# Revit family: vanity unit with 2 drawers for consoles with bowl
name_source: partatom
category: Furniture
units: mm (PartAtom-declared; Revit-internal decimal feet)

## family parameters
Always vertical = Yes
Cut with Voids When Loaded = No
OmniClass Number = 23.21.19.15.33.13
Room Calculation Point = No
Shared = Yes
Work Plane-Based = No

## types (72) — shared parameters
BIMOBJECT = Sanitary: Compound units
CATALOG = Hansgrohe
DESIGN = Germany
ETIM = EC011381 | Bathroom furniture set
IFC = Furnishing element
MASTERFORMAT = 12 35 30.23 | Bathroom Casework
Manufacturer = Hansgrohe
NBSYN = $BASENUMBER.-$ARTNR.-$OBERFLAECHE.-$SURFACE.-$LODLEVEL.
NN = Vanity unit with 2 drawers for consoles with bowl
OBJECTTYPE = Object (single object)
OMNICLASS = 23-21 19 15 33 13 | Residential Bathroom Specialty Casework
PRODUCTFAMILY = Xelu Q
PRODUCTGROUP = vanity unit
PRODUCTURL = https://pro.hansgrohe.com
REGIONSET = Worldwide
UNICLASS2015 = Pr_40_30_78_05 | Bathroom furniture
UNICLASS_2015_CODE = 40_30_78_05
UNIFORMATII = E2010 | Fixed Furnishings
UNSPSC = 56 | Furniture and Furnishings
etim7_EC011381 = EC011381

## per-type parameters (varying)
| type | ARTNR | BASENUMBER | GTINCODE | L | LINA | LODLEVEL | Model | NAME | NB | OBERFLAECHE | PERMALINK | SURFACE | WEIGHT |
| Vanity unit 1180_550 with 2 drawers for consoles with bowl-54082000-High Gloss White-CHROME-200 | 54082000 | Vanity unit 1180/550 with 2 drawers for consoles with bowl | 4059625456699 | 1180 | Vanity unit 1180/550 with 2 drawers for consoles with bowl-54082000-High Gloss White-CHROME-200 | 200 | Vanity unit 1180/550 with 2 drawers for consoles with bowl-54082000-High Gloss White-CHROME-200 | Xelu Q Vanity unit High Gloss White 1180/550 with 2 drawers for consoles with bowl | Vanity unit 1180/550 with 2 drawers for consoles with bowl-54082000-High Gloss White-CHROME-200 | High Gloss White | 54082XXX | CHROME | 42.7 |
| Vanity unit 1180_550 with 2 drawers for consoles with bowl-54082000-High Gloss White-CHROME-400 | 54082000 | Vanity unit 1180/550 with 2 drawers for consoles with bowl | 4059625456699 | 1180 | Vanity unit 1180/550 with 2 drawers for consoles with bowl-54082000-High Gloss White-CHROME-400 | 400 | Vanity unit 1180/550 with 2 drawers for consoles with bowl-54082000-High Gloss White-CHROME-400 | Xelu Q Vanity unit High Gloss White 1180/550 with 2 drawers for consoles with bowl | Vanity unit 1180/550 with 2 drawers for consoles with bowl-54082000-High Gloss White-CHROME-400 | High Gloss White | 54082XXX | CHROME | 42.7 |
| Vanity unit 1180_550 with 2 drawers for consoles with bowl-54082670-High Gloss White-MATT_BLACK-200 | 54082670 | Vanity unit 1180/550 with 2 drawers for consoles with bowl | 4059625456699 | 1180 | Vanity unit 1180/550 with 2 drawers for consoles with bowl-54082670-High Gloss White-MATT_BLACK-200 | 200 | Vanity unit 1180/550 with 2 drawers for consoles with bowl-54082670-High Gloss White-MATT_BLACK-200 | Xelu Q Vanity unit High Gloss White 1180/550 with 2 drawers for consoles with bowl | Vanity unit 1180/550 with 2 drawers for consoles with bowl-54082670-High Gloss White-MATT_BLACK-200 | High Gloss White | 54082XXX | MATT_BLACK | 42.7 |
| Vanity unit 1180_550 with 2 drawers for consoles with bowl-54082670-High Gloss White-MATT_BLACK-400 | 54082670 | Vanity unit 1180/550 with 2 drawers for consoles with bowl | 4059625456699 | 1180 | Vanity unit 1180/550 with 2 drawers for consoles with bowl-54082670-High Gloss White-MATT_BLACK-400 | 400 | Vanity unit 1180/550 with 2 drawers for consoles with bowl-54082670-High Gloss White-MATT_BLACK-400 | Xelu Q Vanity unit High Gloss White 1180/550 with 2 drawers for consoles with bowl | Vanity unit 1180/550 with 2 drawers for consoles with bowl-54082670-High Gloss White-MATT_BLACK-400 | High Gloss White | 54082XXX | MATT_BLACK | 42.7 |
| Vanity unit 1180_550 with 2 drawers for consoles with bowl-54082700-High Gloss White-MATT_WHITE-200 | 54082700 | Vanity unit 1180/550 with 2 drawers for consoles with bowl | 4059625456699 | 1180 | Vanity unit 1180/550 with 2 drawers for consoles with bowl-54082700-High Gloss White-MATT_WHITE-200 | 200 | Vanity unit 1180/550 with 2 drawers for consoles with bowl-54082700-High Gloss White-MATT_WHITE-200 | Xelu Q Vanity unit High Gloss White 1180/550 with 2 drawers for consoles with bowl | Vanity unit 1180/550 with 2 drawers for consoles with bowl-54082700-High Gloss White-MATT_WHITE-200 | High Gloss White | 54082XXX | MATT_WHITE | 42.7 |
| Vanity unit 1180_550 with 2 drawers for consoles with bowl-54082700-High Gloss White-MATT_WHITE-400 | 54082700 | Vanity unit 1180/550 with 2 drawers for consoles with bowl | 4059625456699 | 1180 | Vanity unit 1180/550 with 2 drawers for consoles with bowl-54082700-High Gloss White-MATT_WHITE-400 | 400 | Vanity unit 1180/550 with 2 drawers for consoles with bowl-54082700-High Gloss White-MATT_WHITE-400 | Xelu Q Vanity unit High Gloss White 1180/550 with 2 drawers for consoles with bowl | Vanity unit 1180/550 with 2 drawers for consoles with bowl-54082700-High Gloss White-MATT_WHITE-400 | High Gloss White | 54082XXX | MATT_WHITE | 42.7 |
| Vanity unit 1180_550 with 2 drawers for consoles with bowl-54083000-Diamond Matt Grey-CHROME-200 | 54083000 | Vanity unit 1180/550 with 2 drawers for consoles with bowl | 4059625456668 | 1180 | Vanity unit 1180/550 with 2 drawers for consoles with bowl-54083000-Diamond Matt Grey-CHROME-200 | 200 | Vanity unit 1180/550 with 2 drawers for consoles with bowl-54083000-Diamond Matt Grey-CHROME-200 | Xelu Q Vanity unit Diamond Matt Grey 1180/550 with 2 drawers for consoles with bowl | Vanity unit 1180/550 with 2 drawers for consoles with bowl-54083000-Diamond Matt Grey-CHROME-200 | Diamond Matt Grey | 54083XXX | CHROME | 42.7 |
| Vanity unit 1180_550 with 2 drawers for consoles with bowl-54083000-Diamond Matt Grey-CHROME-400 | 54083000 | Vanity unit 1180/550 with 2 drawers for consoles with bowl | 4059625456668 | 1180 | Vanity unit 1180/550 with 2 drawers for consoles with bowl-54083000-Diamond Matt Grey-CHROME-400 | 400 | Vanity unit 1180/550 with 2 drawers for consoles with bowl-54083000-Diamond Matt Grey-CHROME-400 | Xelu Q Vanity unit Diamond Matt Grey 1180/550 with 2 drawers for consoles with bowl | Vanity unit 1180/550 with 2 drawers for consoles with bowl-54083000-Diamond Matt Grey-CHROME-400 | Diamond Matt Grey | 54083XXX | CHROME | 42.7 |
| Vanity unit 1180_550 with 2 drawers for consoles with bowl-54083670-Diamond Matt Grey-MATT_BLACK-200 | 54083670 | Vanity unit 1180/550 with 2 drawers for consoles with bowl | 4059625456668 | 1180 | Vanity unit 1180/550 with 2 drawers for consoles with bowl-54083670-Diamond Matt Grey-MATT_BLACK-200 | 200 | Vanity unit 1180/550 with 2 drawers for consoles with bowl-54083670-Diamond Matt Grey-MATT_BLACK-200 | Xelu Q Vanity unit Diamond Matt Grey 1180/550 with 2 drawers for consoles with bowl | Vanity unit 1180/550 with 2 drawers for consoles with bowl-54083670-Diamond Matt Grey-MATT_BLACK-200 | Diamond Matt Grey | 54083XXX | MATT_BLACK | 42.7 |
| Vanity unit 1180_550 with 2 drawers for consoles with bowl-54083670-Diamond Matt Grey-MATT_BLACK-400 | 54083670 | Vanity unit 1180/550 with 2 drawers for consoles with bowl | 4059625456668 | 1180 | Vanity unit 1180/550 with 2 drawers for consoles with bowl-54083670-Diamond Matt Grey-MATT_BLACK-400 | 400 | Vanity unit 1180/550 with 2 drawers for consoles with bowl-54083670-Diamond Matt Grey-MATT_BLACK-400 | Xelu Q Vanity unit Diamond Matt Grey 1180/550 with 2 drawers for consoles with bowl | Vanity unit 1180/550 with 2 drawers for consoles with bowl-54083670-Diamond Matt Grey-MATT_BLACK-400 | Diamond Matt Grey | 54083XXX | MATT_BLACK | 42.7 |
| Vanity unit 1180_550 with 2 drawers for consoles with bowl-54083700-Diamond Matt Grey-MATT_WHITE-200 | 54083700 | Vanity unit 1180/550 with 2 drawers for consoles with bowl | 4059625456668 | 1180 | Vanity unit 1180/550 with 2 drawers for consoles with bowl-54083700-Diamond Matt Grey-MATT_WHITE-200 | 200 | Vanity unit 1180/550 with 2 drawers for consoles with bowl-54083700-Diamond Matt Grey-MATT_WHITE-200 | Xelu Q Vanity unit Diamond Matt Grey 1180/550 with 2 drawers for consoles with bowl | Vanity unit 1180/550 with 2 drawers for consoles with bowl-54083700-Diamond Matt Grey-MATT_WHITE-200 | Diamond Matt Grey | 54083XXX | MATT_WHITE | 42.7 |
| Vanity unit 1180_550 with 2 drawers for consoles with bowl-54083700-Diamond Matt Grey-MATT_WHITE-400 | 54083700 | Vanity unit 1180/550 with 2 drawers for consoles with bowl | 4059625456668 | 1180 | Vanity unit 1180/550 with 2 drawers for consoles with bowl-54083700-Diamond Matt Grey-MATT_WHITE-400 | 400 | Vanity unit 1180/550 with 2 drawers for consoles with bowl-54083700-Diamond Matt Grey-MATT_WHITE-400 | Xelu Q Vanity unit Diamond Matt Grey 1180/550 with 2 drawers for consoles with bowl | Vanity unit 1180/550 with 2 drawers for consoles with bowl-54083700-Diamond Matt Grey-MATT_WHITE-400 | Diamond Matt Grey | 54083XXX | MATT_WHITE | 42.7 |
| Vanity unit 1180_550 with 2 drawers for consoles with bowl-54084000-Natural Oak-CHROME-200 | 54084000 | Vanity unit 1180/550 with 2 drawers for consoles with bowl | 4059625457030 | 1180 | Vanity unit 1180/550 with 2 drawers for consoles with bowl-54084000-Natural Oak-CHROME-200 | 200 | Vanity unit 1180/550 with 2 drawers for consoles with bowl-54084000-Natural Oak-CHROME-200 | Xelu Q Vanity unit Natural Oak 1180/550 with 2 drawers for consoles with bowl | Vanity unit 1180/550 with 2 drawers for consoles with bowl-54084000-Natural Oak-CHROME-200 | Natural Oak | 54084XXX | CHROME | 42.7 |
| Vanity unit 1180_550 with 2 drawers for consoles with bowl-54084000-Natural Oak-CHROME-400 | 54084000 | Vanity unit 1180/550 with 2 drawers for consoles with bowl | 4059625457030 | 1180 | Vanity unit 1180/550 with 2 drawers for consoles with bowl-54084000-Natural Oak-CHROME-400 | 400 | Vanity unit 1180/550 with 2 drawers for consoles with bowl-54084000-Natural Oak-CHROME-400 | Xelu Q Vanity unit Natural Oak 1180/550 with 2 drawers for consoles with bowl | Vanity unit 1180/550 with 2 drawers for consoles with bowl-54084000-Natural Oak-CHROME-400 | Natural Oak | 54084XXX | CHROME | 42.7 |
| Vanity unit 1180_550 with 2 drawers for consoles with bowl-54084670-Natural Oak-MATT_BLACK-200 | 54084670 | Vanity unit 1180/550 with 2 drawers for consoles with bowl | 4059625457030 | 1180 | Vanity unit 1180/550 with 2 drawers for consoles with bowl-54084670-Natural Oak-MATT_BLACK-200 | 200 | Vanity unit 1180/550 with 2 drawers for consoles with bowl-54084670-Natural Oak-MATT_BLACK-200 | Xelu Q Vanity unit Natural Oak 1180/550 with 2 drawers for consoles with bowl | Vanity unit 1180/550 with 2 drawers for consoles with bowl-54084670-Natural Oak-MATT_BLACK-200 | Natural Oak | 54084XXX | MATT_BLACK | 42.7 |
| Vanity unit 1180_550 with 2 drawers for consoles with bowl-54084670-Natural Oak-MATT_BLACK-400 | 54084670 | Vanity unit 1180/550 with 2 drawers for consoles with bowl | 4059625457030 | 1180 | Vanity unit 1180/550 with 2 drawers for consoles with bowl-54084670-Natural Oak-MATT_BLACK-400 | 400 | Vanity unit 1180/550 with 2 drawers for consoles with bowl-54084670-Natural Oak-MATT_BLACK-400 | Xelu Q Vanity unit Natural Oak 1180/550 with 2 drawers for consoles with bowl | Vanity unit 1180/550 with 2 drawers for consoles with bowl-54084670-Natural Oak-MATT_BLACK-400 | Natural Oak | 54084XXX | MATT_BLACK | 42.7 |
| Vanity unit 1180_550 with 2 drawers for consoles with bowl-54084700-Natural Oak-MATT_WHITE-200 | 54084700 | Vanity unit 1180/550 with 2 drawers for consoles with bowl | 4059625457030 | 1180 | Vanity unit 1180/550 with 2 drawers for consoles with bowl-54084700-Natural Oak-MATT_WHITE-200 | 200 | Vanity unit 1180/550 with 2 drawers for consoles with bowl-54084700-Natural Oak-MATT_WHITE-200 | Xelu Q Vanity unit Natural Oak 1180/550 with 2 drawers for consoles with bowl | Vanity unit 1180/550 with 2 drawers for consoles with bowl-54084700-Natural Oak-MATT_WHITE-200 | Natural Oak | 54084XXX | MATT_WHITE | 42.7 |
| Vanity unit 1180_550 with 2 drawers for consoles with bowl-54084700-Natural Oak-MATT_WHITE-400 | 54084700 | Vanity unit 1180/550 with 2 drawers for consoles with bowl | 4059625457030 | 1180 | Vanity unit 1180/550 with 2 drawers for consoles with bowl-54084700-Natural Oak-MATT_WHITE-400 | 400 | Vanity unit 1180/550 with 2 drawers for consoles with bowl-54084700-Natural Oak-MATT_WHITE-400 | Xelu Q Vanity unit Natural Oak 1180/550 with 2 drawers for consoles with bowl | Vanity unit 1180/550 with 2 drawers for consoles with bowl-54084700-Natural Oak-MATT_WHITE-400 | Natural Oak | 54084XXX | MATT_WHITE | 42.7 |
| Vanity unit 1180_550 with 2 drawers for consoles with bowl-54085000-Dark Walnut-CHROME-200 | 54085000 | Vanity unit 1180/550 with 2 drawers for consoles with bowl | 4059625457009 | 1180 | Vanity unit 1180/550 with 2 drawers for consoles with bowl-54085000-Dark Walnut-CHROME-200 | 200 | Vanity unit 1180/550 with 2 drawers for consoles with bowl-54085000-Dark Walnut-CHROME-200 | Xelu Q Vanity unit Dark Walnut 1180/550 with 2 drawers for consoles with bowl | Vanity unit 1180/550 with 2 drawers for consoles with bowl-54085000-Dark Walnut-CHROME-200 | Dark Walnut | 54085XXX | CHROME | 42.7 |
| Vanity unit 1180_550 with 2 drawers for consoles with bowl-54085000-Dark Walnut-CHROME-400 | 54085000 | Vanity unit 1180/550 with 2 drawers for consoles with bowl | 4059625457009 | 1180 | Vanity unit 1180/550 with 2 drawers for consoles with bowl-54085000-Dark Walnut-CHROME-400 | 400 | Vanity unit 1180/550 with 2 drawers for consoles with bowl-54085000-Dark Walnut-CHROME-400 | Xelu Q Vanity unit Dark Walnut 1180/550 with 2 drawers for consoles with bowl | Vanity unit 1180/550 with 2 drawers for consoles with bowl-54085000-Dark Walnut-CHROME-400 | Dark Walnut | 54085XXX | CHROME | 42.7 |
| Vanity unit 1180_550 with 2 drawers for consoles with bowl-54085670-Dark Walnut-MATT_BLACK-200 | 54085670 | Vanity unit 1180/550 with 2 drawers for consoles with bowl | 4059625457009 | 1180 | Vanity unit 1180/550 with 2 drawers for consoles with bowl-54085670-Dark Walnut-MATT_BLACK-200 | 200 | Vanity unit 1180/550 with 2 drawers for consoles with bowl-54085670-Dark Walnut-MATT_BLACK-200 | Xelu Q Vanity unit Dark Walnut 1180/550 with 2 drawers for consoles with bowl | Vanity unit 1180/550 with 2 drawers for consoles with bowl-54085670-Dark Walnut-MATT_BLACK-200 | Dark Walnut | 54085XXX | MATT_BLACK | 42.7 |
| Vanity unit 1180_550 with 2 drawers for consoles with bowl-54085670-Dark Walnut-MATT_BLACK-400 | 54085670 | Vanity unit 1180/550 with 2 drawers for consoles with bowl | 4059625457009 | 1180 | Vanity unit 1180/550 with 2 drawers for consoles with bowl-54085670-Dark Walnut-MATT_BLACK-400 | 400 | Vanity unit 1180/550 with 2 drawers for consoles with bowl-54085670-Dark Walnut-MATT_BLACK-400 | Xelu Q Vanity unit Dark Walnut 1180/550 with 2 drawers for consoles with bowl | Vanity unit 1180/550 with 2 drawers for consoles with bowl-54085670-Dark Walnut-MATT_BLACK-400 | Dark Walnut | 54085XXX | MATT_BLACK | 42.7 |
| Vanity unit 1180_550 with 2 drawers for consoles with bowl-54085700-Dark Walnut-MATT_WHITE-200 | 54085700 | Vanity unit 1180/550 with 2 drawers for consoles with bowl | 4059625457009 | 1180 | Vanity unit 1180/550 with 2 drawers for consoles with bowl-54085700-Dark Walnut-MATT_WHITE-200 | 200 | Vanity unit 1180/550 with 2 drawers for consoles with bowl-54085700-Dark Walnut-MATT_WHITE-200 | Xelu Q Vanity unit Dark Walnut 1180/550 with 2 drawers for consoles with bowl | Vanity unit 1180/550 with 2 drawers for consoles with bowl-54085700-Dark Walnut-MATT_WHITE-200 | Dark Walnut | 54085XXX | MATT_WHITE | 42.7 |
| Vanity unit 1180_550 with 2 drawers for consoles with bowl-54085700-Dark Walnut-MATT_WHITE-400 | 54085700 | Vanity unit 1180/550 with 2 drawers for consoles with bowl | 4059625457009 | 1180 | Vanity unit 1180/550 with 2 drawers for consoles with bowl-54085700-Dark Walnut-MATT_WHITE-400 | 400 | Vanity unit 1180/550 with 2 drawers for consoles with bowl-54085700-Dark Walnut-MATT_WHITE-400 | Xelu Q Vanity unit Dark Walnut 1180/550 with 2 drawers for consoles with bowl | Vanity unit 1180/550 with 2 drawers for consoles with bowl-54085700-Dark Walnut-MATT_WHITE-400 | Dark Walnut | 54085XXX | MATT_WHITE | 42.7 |
| Vanity unit 780_550 with 2 drawers for consoles with bowl-54074000-High Gloss White-CHROME-200 | 54074000 | Vanity unit 780/550 with 2 drawers for consoles with bowl | 4059625456538 | 780 | Vanity unit 780/550 with 2 drawers for consoles with bowl-54074000-High Gloss White-CHROME-200 | 200 | Vanity unit 780/550 with 2 drawers for consoles with bowl-54074000-High Gloss White-CHROME-200 | Xelu Q Vanity unit High Gloss White 780/550 with 2 drawers for consoles with bowl | Vanity unit 780/550 with 2 drawers for consoles with bowl-54074000-High Gloss White-CHROME-200 | High Gloss White | 54074XXX | CHROME | 31.3 |
| Vanity unit 780_550 with 2 drawers for consoles with bowl-54074000-High Gloss White-CHROME-400 | 54074000 | Vanity unit 780/550 with 2 drawers for consoles with bowl | 4059625456538 | 780 | Vanity unit 780/550 with 2 drawers for consoles with bowl-54074000-High Gloss White-CHROME-400 | 400 | Vanity unit 780/550 with 2 drawers for consoles with bowl-54074000-High Gloss White-CHROME-400 | Xelu Q Vanity unit High Gloss White 780/550 with 2 drawers for consoles with bowl | Vanity unit 780/550 with 2 drawers for consoles with bowl-54074000-High Gloss White-CHROME-400 | High Gloss White | 54074XXX | CHROME | 31.3 |
| Vanity unit 780_550 with 2 drawers for consoles with bowl-54074670-High Gloss White-MATT_BLACK-200 | 54074670 | Vanity unit 780/550 with 2 drawers for consoles with bowl | 4059625456538 | 780 | Vanity unit 780/550 with 2 drawers for consoles with bowl-54074670-High Gloss White-MATT_BLACK-200 | 200 | Vanity unit 780/550 with 2 drawers for consoles with bowl-54074670-High Gloss White-MATT_BLACK-200 | Xelu Q Vanity unit High Gloss White 780/550 with 2 drawers for consoles with bowl | Vanity unit 780/550 with 2 drawers for consoles with bowl-54074670-High Gloss White-MATT_BLACK-200 | High Gloss White | 54074XXX | MATT_BLACK | 31.3 |
| Vanity unit 780_550 with 2 drawers for consoles with bowl-54074670-High Gloss White-MATT_BLACK-400 | 54074670 | Vanity unit 780/550 with 2 drawers for consoles with bowl | 4059625456538 | 780 | Vanity unit 780/550 with 2 drawers for consoles with bowl-54074670-High Gloss White-MATT_BLACK-400 | 400 | Vanity unit 780/550 with 2 drawers for consoles with bowl-54074670-High Gloss White-MATT_BLACK-400 | Xelu Q Vanity unit High Gloss White 780/550 with 2 drawers for consoles with bowl | Vanity unit 780/550 with 2 drawers for consoles with bowl-54074670-High Gloss White-MATT_BLACK-400 | High Gloss White | 54074XXX | MATT_BLACK | 31.3 |
| Vanity unit 780_550 with 2 drawers for consoles with bowl-54074700-High Gloss White-MATT_WHITE-200 | 54074700 | Vanity unit 780/550 with 2 drawers for consoles with bowl | 4059625456538 | 780 | Vanity unit 780/550 with 2 drawers for consoles with bowl-54074700-High Gloss White-MATT_WHITE-200 | 200 | Vanity unit 780/550 with 2 drawers for consoles with bowl-54074700-High Gloss White-MATT_WHITE-200 | Xelu Q Vanity unit High Gloss White 780/550 with 2 drawers for consoles with bowl | Vanity unit 780/550 with 2 drawers for consoles with bowl-54074700-High Gloss White-MATT_WHITE-200 | High Gloss White | 54074XXX | MATT_WHITE | 31.3 |
| Vanity unit 780_550 with 2 drawers for consoles with bowl-54074700-High Gloss White-MATT_WHITE-400 | 54074700 | Vanity unit 780/550 with 2 drawers for consoles with bowl | 4059625456538 | 780 | Vanity unit 780/550 with 2 drawers for consoles with bowl-54074700-High Gloss White-MATT_WHITE-400 | 400 | Vanity unit 780/550 with 2 drawers for consoles with bowl-54074700-High Gloss White-MATT_WHITE-400 | Xelu Q Vanity unit High Gloss White 780/550 with 2 drawers for consoles with bowl | Vanity unit 780/550 with 2 drawers for consoles with bowl-54074700-High Gloss White-MATT_WHITE-400 | High Gloss White | 54074XXX | MATT_WHITE | 31.3 |
| Vanity unit 780_550 with 2 drawers for consoles with bowl-54075000-Diamond Matt Grey-CHROME-200 | 54075000 | Vanity unit 780/550 with 2 drawers for consoles with bowl | 4059625456507 | 780 | Vanity unit 780/550 with 2 drawers for consoles with bowl-54075000-Diamond Matt Grey-CHROME-200 | 200 | Vanity unit 780/550 with 2 drawers for consoles with bowl-54075000-Diamond Matt Grey-CHROME-200 | Xelu Q Vanity unit Diamond Matt Grey 780/550 with 2 drawers for consoles with bowl | Vanity unit 780/550 with 2 drawers for consoles with bowl-54075000-Diamond Matt Grey-CHROME-200 | Diamond Matt Grey | 54075XXX | CHROME | 31.3 |
| Vanity unit 780_550 with 2 drawers for consoles with bowl-54075000-Diamond Matt Grey-CHROME-400 | 54075000 | Vanity unit 780/550 with 2 drawers for consoles with bowl | 4059625456507 | 780 | Vanity unit 780/550 with 2 drawers for consoles with bowl-54075000-Diamond Matt Grey-CHROME-400 | 400 | Vanity unit 780/550 with 2 drawers for consoles with bowl-54075000-Diamond Matt Grey-CHROME-400 | Xelu Q Vanity unit Diamond Matt Grey 780/550 with 2 drawers for consoles with bowl | Vanity unit 780/550 with 2 drawers for consoles with bowl-54075000-Diamond Matt Grey-CHROME-400 | Diamond Matt Grey | 54075XXX | CHROME | 31.3 |
| Vanity unit 780_550 with 2 drawers for consoles with bowl-54075670-Diamond Matt Grey-MATT_BLACK-200 | 54075670 | Vanity unit 780/550 with 2 drawers for consoles with bowl | 4059625456507 | 780 | Vanity unit 780/550 with 2 drawers for consoles with bowl-54075670-Diamond Matt Grey-MATT_BLACK-200 | 200 | Vanity unit 780/550 with 2 drawers for consoles with bowl-54075670-Diamond Matt Grey-MATT_BLACK-200 | Xelu Q Vanity unit Diamond Matt Grey 780/550 with 2 drawers for consoles with bowl | Vanity unit 780/550 with 2 drawers for consoles with bowl-54075670-Diamond Matt Grey-MATT_BLACK-200 | Diamond Matt Grey | 54075XXX | MATT_BLACK | 31.3 |
| Vanity unit 780_550 with 2 drawers for consoles with bowl-54075670-Diamond Matt Grey-MATT_BLACK-400 | 54075670 | Vanity unit 780/550 with 2 drawers for consoles with bowl | 4059625456507 | 780 | Vanity unit 780/550 with 2 drawers for consoles with bowl-54075670-Diamond Matt Grey-MATT_BLACK-400 | 400 | Vanity unit 780/550 with 2 drawers for consoles with bowl-54075670-Diamond Matt Grey-MATT_BLACK-400 | Xelu Q Vanity unit Diamond Matt Grey 780/550 with 2 drawers for consoles with bowl | Vanity unit 780/550 with 2 drawers for consoles with bowl-54075670-Diamond Matt Grey-MATT_BLACK-400 | Diamond Matt Grey | 54075XXX | MATT_BLACK | 31.3 |
| Vanity unit 780_550 with 2 drawers for consoles with bowl-54075700-Diamond Matt Grey-MATT_WHITE-200 | 54075700 | Vanity unit 780/550 with 2 drawers for consoles with bowl | 4059625456507 | 780 | Vanity unit 780/550 with 2 drawers for consoles with bowl-54075700-Diamond Matt Grey-MATT_WHITE-200 | 200 | Vanity unit 780/550 with 2 drawers for consoles with bowl-54075700-Diamond Matt Grey-MATT_WHITE-200 | Xelu Q Vanity unit Diamond Matt Grey 780/550 with 2 drawers for consoles with bowl | Vanity unit 780/550 with 2 drawers for consoles with bowl-54075700-Diamond Matt Grey-MATT_WHITE-200 | Diamond Matt Grey | 54075XXX | MATT_WHITE | 31.3 |
| Vanity unit 780_550 with 2 drawers for consoles with bowl-54075700-Diamond Matt Grey-MATT_WHITE-400 | 54075700 | Vanity unit 780/550 with 2 drawers for consoles with bowl | 4059625456507 | 780 | Vanity unit 780/550 with 2 drawers for consoles with bowl-54075700-Diamond Matt Grey-MATT_WHITE-400 | 400 | Vanity unit 780/550 with 2 drawers for consoles with bowl-54075700-Diamond Matt Grey-MATT_WHITE-400 | Xelu Q Vanity unit Diamond Matt Grey 780/550 with 2 drawers for consoles with bowl | Vanity unit 780/550 with 2 drawers for consoles with bowl-54075700-Diamond Matt Grey-MATT_WHITE-400 | Diamond Matt Grey | 54075XXX | MATT_WHITE | 31.3 |
| Vanity unit 780_550 with 2 drawers for consoles with bowl-54076000-Natural Oak-CHROME-200 | 54076000 | Vanity unit 780/550 with 2 drawers for consoles with bowl | 4059625456477 | 780 | Vanity unit 780/550 with 2 drawers for consoles with bowl-54076000-Natural Oak-CHROME-200 | 200 | Vanity unit 780/550 with 2 drawers for consoles with bowl-54076000-Natural Oak-CHROME-200 | Xelu Q Vanity unit Natural Oak 780/550 with 2 drawers for consoles with bowl | Vanity unit 780/550 with 2 drawers for consoles with bowl-54076000-Natural Oak-CHROME-200 | Natural Oak | 54076XXX | CHROME | 31.3 |
| Vanity unit 780_550 with 2 drawers for consoles with bowl-54076000-Natural Oak-CHROME-400 | 54076000 | Vanity unit 780/550 with 2 drawers for consoles with bowl | 4059625456477 | 780 | Vanity unit 780/550 with 2 drawers for consoles with bowl-54076000-Natural Oak-CHROME-400 | 400 | Vanity unit 780/550 with 2 drawers for consoles with bowl-54076000-Natural Oak-CHROME-400 | Xelu Q Vanity unit Natural Oak 780/550 with 2 drawers for consoles with bowl | Vanity unit 780/550 with 2 drawers for consoles with bowl-54076000-Natural Oak-CHROME-400 | Natural Oak | 54076XXX | CHROME | 31.3 |
| Vanity unit 780_550 with 2 drawers for consoles with bowl-54076670-Natural Oak-MATT_BLACK-200 | 54076670 | Vanity unit 780/550 with 2 drawers for consoles with bowl | 4059625456477 | 780 | Vanity unit 780/550 with 2 drawers for consoles with bowl-54076670-Natural Oak-MATT_BLACK-200 | 200 | Vanity unit 780/550 with 2 drawers for consoles with bowl-54076670-Natural Oak-MATT_BLACK-200 | Xelu Q Vanity unit Natural Oak 780/550 with 2 drawers for consoles with bowl | Vanity unit 780/550 with 2 drawers for consoles with bowl-54076670-Natural Oak-MATT_BLACK-200 | Natural Oak | 54076XXX | MATT_BLACK | 31.3 |
| Vanity unit 780_550 with 2 drawers for consoles with bowl-54076670-Natural Oak-MATT_BLACK-400 | 54076670 | Vanity unit 780/550 with 2 drawers for consoles with bowl | 4059625456477 | 780 | Vanity unit 780/550 with 2 drawers for consoles with bowl-54076670-Natural Oak-MATT_BLACK-400 | 400 | Vanity unit 780/550 with 2 drawers for consoles with bowl-54076670-Natural Oak-MATT_BLACK-400 | Xelu Q Vanity unit Natural Oak 780/550 with 2 drawers for consoles with bowl | Vanity unit 780/550 with 2 drawers for consoles with bowl-54076670-Natural Oak-MATT_BLACK-400 | Natural Oak | 54076XXX | MATT_BLACK | 31.3 |
| Vanity unit 780_550 with 2 drawers for consoles with bowl-54076700-Natural Oak-MATT_WHITE-200 | 54076700 | Vanity unit 780/550 with 2 drawers for consoles with bowl | 4059625456477 | 780 | Vanity unit 780/550 with 2 drawers for consoles with bowl-54076700-Natural Oak-MATT_WHITE-200 | 200 | Vanity unit 780/550 with 2 drawers for consoles with bowl-54076700-Natural Oak-MATT_WHITE-200 | Xelu Q Vanity unit Natural Oak 780/550 with 2 drawers for consoles with bowl | Vanity unit 780/550 with 2 drawers for consoles with bowl-54076700-Natural Oak-MATT_WHITE-200 | Natural Oak | 54076XXX | MATT_WHITE | 31.3 |
| Vanity unit 780_550 with 2 drawers for consoles with bowl-54076700-Natural Oak-MATT_WHITE-400 | 54076700 | Vanity unit 780/550 with 2 drawers for consoles with bowl | 4059625456477 | 780 | Vanity unit 780/550 with 2 drawers for consoles with bowl-54076700-Natural Oak-MATT_WHITE-400 | 400 | Vanity unit 780/550 with 2 drawers for consoles with bowl-54076700-Natural Oak-MATT_WHITE-400 | Xelu Q Vanity unit Natural Oak 780/550 with 2 drawers for consoles with bowl | Vanity unit 780/550 with 2 drawers for consoles with bowl-54076700-Natural Oak-MATT_WHITE-400 | Natural Oak | 54076XXX | MATT_WHITE | 31.3 |
| Vanity unit 780_550 with 2 drawers for consoles with bowl-54077000-Dark Walnut-CHROME-200 | 54077000 | Vanity unit 780/550 with 2 drawers for consoles with bowl | 4059625456446 | 780 | Vanity unit 780/550 with 2 drawers for consoles with bowl-54077000-Dark Walnut-CHROME-200 | 200 | Vanity unit 780/550 with 2 drawers for consoles with bowl-54077000-Dark Walnut-CHROME-200 | Xelu Q Vanity unit Dark Walnut 780/550 with 2 drawers for consoles with bowl | Vanity unit 780/550 with 2 drawers for consoles with bowl-54077000-Dark Walnut-CHROME-200 | Dark Walnut | 54077XXX | CHROME | 31.3 |
| Vanity unit 780_550 with 2 drawers for consoles with bowl-54077000-Dark Walnut-CHROME-400 | 54077000 | Vanity unit 780/550 with 2 drawers for consoles with bowl | 4059625456446 | 780 | Vanity unit 780/550 with 2 drawers for consoles with bowl-54077000-Dark Walnut-CHROME-400 | 400 | Vanity unit 780/550 with 2 drawers for consoles with bowl-54077000-Dark Walnut-CHROME-400 | Xelu Q Vanity unit Dark Walnut 780/550 with 2 drawers for consoles with bowl | Vanity unit 780/550 with 2 drawers for consoles with bowl-54077000-Dark Walnut-CHROME-400 | Dark Walnut | 54077XXX | CHROME | 31.3 |
| Vanity unit 780_550 with 2 drawers for consoles with bowl-54077670-Dark Walnut-MATT_BLACK-200 | 54077670 | Vanity unit 780/550 with 2 drawers for consoles with bowl | 4059625456446 | 780 | Vanity unit 780/550 with 2 drawers for consoles with bowl-54077670-Dark Walnut-MATT_BLACK-200 | 200 | Vanity unit 780/550 with 2 drawers for consoles with bowl-54077670-Dark Walnut-MATT_BLACK-200 | Xelu Q Vanity unit Dark Walnut 780/550 with 2 drawers for consoles with bowl | Vanity unit 780/550 with 2 drawers for consoles with bowl-54077670-Dark Walnut-MATT_BLACK-200 | Dark Walnut | 54077XXX | MATT_BLACK | 31.3 |
| Vanity unit 780_550 with 2 drawers for consoles with bowl-54077670-Dark Walnut-MATT_BLACK-400 | 54077670 | Vanity unit 780/550 with 2 drawers for consoles with bowl | 4059625456446 | 780 | Vanity unit 780/550 with 2 drawers for consoles with bowl-54077670-Dark Walnut-MATT_BLACK-400 | 400 | Vanity unit 780/550 with 2 drawers for consoles with bowl-54077670-Dark Walnut-MATT_BLACK-400 | Xelu Q Vanity unit Dark Walnut 780/550 with 2 drawers for consoles with bowl | Vanity unit 780/550 with 2 drawers for consoles with bowl-54077670-Dark Walnut-MATT_BLACK-400 | Dark Walnut | 54077XXX | MATT_BLACK | 31.3 |
| Vanity unit 780_550 with 2 drawers for consoles with bowl-54077700-Dark Walnut-MATT_WHITE-200 | 54077700 | Vanity unit 780/550 with 2 drawers for consoles with bowl | 4059625456446 | 780 | Vanity unit 780/550 with 2 drawers for consoles with bowl-54077700-Dark Walnut-MATT_WHITE-200 | 200 | Vanity unit 780/550 with 2 drawers for consoles with bowl-54077700-Dark Walnut-MATT_WHITE-200 | Xelu Q Vanity unit Dark Walnut 780/550 with 2 drawers for consoles with bowl | Vanity unit 780/550 with 2 drawers for consoles with bowl-54077700-Dark Walnut-MATT_WHITE-200 | Dark Walnut | 54077XXX | MATT_WHITE | 31.3 |
| Vanity unit 780_550 with 2 drawers for consoles with bowl-54077700-Dark Walnut-MATT_WHITE-400 | 54077700 | Vanity unit 780/550 with 2 drawers for consoles with bowl | 4059625456446 | 780 | Vanity unit 780/550 with 2 drawers for consoles with bowl-54077700-Dark Walnut-MATT_WHITE-400 | 400 | Vanity unit 780/550 with 2 drawers for consoles with bowl-54077700-Dark Walnut-MATT_WHITE-400 | Xelu Q Vanity unit Dark Walnut 780/550 with 2 drawers for consoles with bowl | Vanity unit 780/550 with 2 drawers for consoles with bowl-54077700-Dark Walnut-MATT_WHITE-400 | Dark Walnut | 54077XXX | MATT_WHITE | 31.3 |
| Vanity unit 980_550 with 2 drawers for consoles with bowl-54078000-High Gloss White-CHROME-200 | 54078000 | Vanity unit 980/550 with 2 drawers for consoles with bowl | 4059625456811 | 980 | Vanity unit 980/550 with 2 drawers for consoles with bowl-54078000-High Gloss White-CHROME-200 | 200 | Vanity unit 980/550 with 2 drawers for consoles with bowl-54078000-High Gloss White-CHROME-200 | Xelu Q Vanity unit High Gloss White 980/550 with 2 drawers for consoles with bowl | Vanity unit 980/550 with 2 drawers for consoles with bowl-54078000-High Gloss White-CHROME-200 | High Gloss White | 54078XXX | CHROME | 37.4 |
| Vanity unit 980_550 with 2 drawers for consoles with bowl-54078000-High Gloss White-CHROME-400 | 54078000 | Vanity unit 980/550 with 2 drawers for consoles with bowl | 4059625456811 | 980 | Vanity unit 980/550 with 2 drawers for consoles with bowl-54078000-High Gloss White-CHROME-400 | 400 | Vanity unit 980/550 with 2 drawers for consoles with bowl-54078000-High Gloss White-CHROME-400 | Xelu Q Vanity unit High Gloss White 980/550 with 2 drawers for consoles with bowl | Vanity unit 980/550 with 2 drawers for consoles with bowl-54078000-High Gloss White-CHROME-400 | High Gloss White | 54078XXX | CHROME | 37.4 |
| Vanity unit 980_550 with 2 drawers for consoles with bowl-54078670-High Gloss White-MATT_BLACK-200 | 54078670 | Vanity unit 980/550 with 2 drawers for consoles with bowl | 4059625456811 | 980 | Vanity unit 980/550 with 2 drawers for consoles with bowl-54078670-High Gloss White-MATT_BLACK-200 | 200 | Vanity unit 980/550 with 2 drawers for consoles with bowl-54078670-High Gloss White-MATT_BLACK-200 | Xelu Q Vanity unit High Gloss White 980/550 with 2 drawers for consoles with bowl | Vanity unit 980/550 with 2 drawers for consoles with bowl-54078670-High Gloss White-MATT_BLACK-200 | High Gloss White | 54078XXX | MATT_BLACK | 37.4 |
| Vanity unit 980_550 with 2 drawers for consoles with bowl-54078670-High Gloss White-MATT_BLACK-400 | 54078670 | Vanity unit 980/550 with 2 drawers for consoles with bowl | 4059625456811 | 980 | Vanity unit 980/550 with 2 drawers for consoles with bowl-54078670-High Gloss White-MATT_BLACK-400 | 400 | Vanity unit 980/550 with 2 drawers for consoles with bowl-54078670-High Gloss White-MATT_BLACK-400 | Xelu Q Vanity unit High Gloss White 980/550 with 2 drawers for consoles with bowl | Vanity unit 980/550 with 2 drawers for consoles with bowl-54078670-High Gloss White-MATT_BLACK-400 | High Gloss White | 54078XXX | MATT_BLACK | 37.4 |
| Vanity unit 980_550 with 2 drawers for consoles with bowl-54078700-High Gloss White-MATT_WHITE-200 | 54078700 | Vanity unit 980/550 with 2 drawers for consoles with bowl | 4059625456811 | 980 | Vanity unit 980/550 with 2 drawers for consoles with bowl-54078700-High Gloss White-MATT_WHITE-200 | 200 | Vanity unit 980/550 with 2 drawers for consoles with bowl-54078700-High Gloss White-MATT_WHITE-200 | Xelu Q Vanity unit High Gloss White 980/550 with 2 drawers for consoles with bowl | Vanity unit 980/550 with 2 drawers for consoles with bowl-54078700-High Gloss White-MATT_WHITE-200 | High Gloss White | 54078XXX | MATT_WHITE | 37.4 |
| Vanity unit 980_550 with 2 drawers for consoles with bowl-54078700-High Gloss White-MATT_WHITE-400 | 54078700 | Vanity unit 980/550 with 2 drawers for consoles with bowl | 4059625456811 | 980 | Vanity unit 980/550 with 2 drawers for consoles with bowl-54078700-High Gloss White-MATT_WHITE-400 | 400 | Vanity unit 980/550 with 2 drawers for consoles with bowl-54078700-High Gloss White-MATT_WHITE-400 | Xelu Q Vanity unit High Gloss White 980/550 with 2 drawers for consoles with bowl | Vanity unit 980/550 with 2 drawers for consoles with bowl-54078700-High Gloss White-MATT_WHITE-400 | High Gloss White | 54078XXX | MATT_WHITE | 37.4 |
| Vanity unit 980_550 with 2 drawers for consoles with bowl-54079000-Diamond Matt Grey-CHROME-200 | 54079000 | Vanity unit 980/550 with 2 drawers for consoles with bowl | 4059625456781 | 980 | Vanity unit 980/550 with 2 drawers for consoles with bowl-54079000-Diamond Matt Grey-CHROME-200 | 200 | Vanity unit 980/550 with 2 drawers for consoles with bowl-54079000-Diamond Matt Grey-CHROME-200 | Xelu Q Vanity unit Diamond Matt Grey 980/550 with 2 drawers for consoles with bowl | Vanity unit 980/550 with 2 drawers for consoles with bowl-54079000-Diamond Matt Grey-CHROME-200 | Diamond Matt Grey | 54079XXX | CHROME | 37.4 |
| Vanity unit 980_550 with 2 drawers for consoles with bowl-54079000-Diamond Matt Grey-CHROME-400 | 54079000 | Vanity unit 980/550 with 2 drawers for consoles with bowl | 4059625456781 | 980 | Vanity unit 980/550 with 2 drawers for consoles with bowl-54079000-Diamond Matt Grey-CHROME-400 | 400 | Vanity unit 980/550 with 2 drawers for consoles with bowl-54079000-Diamond Matt Grey-CHROME-400 | Xelu Q Vanity unit Diamond Matt Grey 980/550 with 2 drawers for consoles with bowl | Vanity unit 980/550 with 2 drawers for consoles with bowl-54079000-Diamond Matt Grey-CHROME-400 | Diamond Matt Grey | 54079XXX | CHROME | 37.4 |
| Vanity unit 980_550 with 2 drawers for consoles with bowl-54079670-Diamond Matt Grey-MATT_BLACK-200 | 54079670 | Vanity unit 980/550 with 2 drawers for consoles with bowl | 4059625456781 | 980 | Vanity unit 980/550 with 2 drawers for consoles with bowl-54079670-Diamond Matt Grey-MATT_BLACK-200 | 200 | Vanity unit 980/550 with 2 drawers for consoles with bowl-54079670-Diamond Matt Grey-MATT_BLACK-200 | Xelu Q Vanity unit Diamond Matt Grey 980/550 with 2 drawers for consoles with bowl | Vanity unit 980/550 with 2 drawers for consoles with bowl-54079670-Diamond Matt Grey-MATT_BLACK-200 | Diamond Matt Grey | 54079XXX | MATT_BLACK | 37.4 |
| Vanity unit 980_550 with 2 drawers for consoles with bowl-54079670-Diamond Matt Grey-MATT_BLACK-400 | 54079670 | Vanity unit 980/550 with 2 drawers for consoles with bowl | 4059625456781 | 980 | Vanity unit 980/550 with 2 drawers for consoles with bowl-54079670-Diamond Matt Grey-MATT_BLACK-400 | 400 | Vanity unit 980/550 with 2 drawers for consoles with bowl-54079670-Diamond Matt Grey-MATT_BLACK-400 | Xelu Q Vanity unit Diamond Matt Grey 980/550 with 2 drawers for consoles with bowl | Vanity unit 980/550 with 2 drawers for consoles with bowl-54079670-Diamond Matt Grey-MATT_BLACK-400 | Diamond Matt Grey | 54079XXX | MATT_BLACK | 37.4 |
| Vanity unit 980_550 with 2 drawers for consoles with bowl-54079700-Diamond Matt Grey-MATT_WHITE-200 | 54079700 | Vanity unit 980/550 with 2 drawers for consoles with bowl | 4059625456781 | 980 | Vanity unit 980/550 with 2 drawers for consoles with bowl-54079700-Diamond Matt Grey-MATT_WHITE-200 | 200 | Vanity unit 980/550 with 2 drawers for consoles with bowl-54079700-Diamond Matt Grey-MATT_WHITE-200 | Xelu Q Vanity unit Diamond Matt Grey 980/550 with 2 drawers for consoles with bowl | Vanity unit 980/550 with 2 drawers for consoles with bowl-54079700-Diamond Matt Grey-MATT_WHITE-200 | Diamond Matt Grey | 54079XXX | MATT_WHITE | 37.4 |
| Vanity unit 980_550 with 2 drawers for consoles with bowl-54079700-Diamond Matt Grey-MATT_WHITE-400 | 54079700 | Vanity unit 980/550 with 2 drawers for consoles with bowl | 4059625456781 | 980 | Vanity unit 980/550 with 2 drawers for consoles with bowl-54079700-Diamond Matt Grey-MATT_WHITE-400 | 400 | Vanity unit 980/550 with 2 drawers for consoles with bowl-54079700-Diamond Matt Grey-MATT_WHITE-400 | Xelu Q Vanity unit Diamond Matt Grey 980/550 with 2 drawers for consoles with bowl | Vanity unit 980/550 with 2 drawers for consoles with bowl-54079700-Diamond Matt Grey-MATT_WHITE-400 | Diamond Matt Grey | 54079XXX | MATT_WHITE | 37.4 |
| Vanity unit 980_550 with 2 drawers for consoles with bowl-54080000-Natural Oak-CHROME-200 | 54080000 | Vanity unit 980/550 with 2 drawers for consoles with bowl | 4059625456750 | 980 | Vanity unit 980/550 with 2 drawers for consoles with bowl-54080000-Natural Oak-CHROME-200 | 200 | Vanity unit 980/550 with 2 drawers for consoles with bowl-54080000-Natural Oak-CHROME-200 | Xelu Q Vanity unit Natural Oak 980/550 with 2 drawers for consoles with bowl | Vanity unit 980/550 with 2 drawers for consoles with bowl-54080000-Natural Oak-CHROME-200 | Natural Oak | 54080XXX | CHROME | 37.4 |
| Vanity unit 980_550 with 2 drawers for consoles with bowl-54080000-Natural Oak-CHROME-400 | 54080000 | Vanity unit 980/550 with 2 drawers for consoles with bowl | 4059625456750 | 980 | Vanity unit 980/550 with 2 drawers for consoles with bowl-54080000-Natural Oak-CHROME-400 | 400 | Vanity unit 980/550 with 2 drawers for consoles with bowl-54080000-Natural Oak-CHROME-400 | Xelu Q Vanity unit Natural Oak 980/550 with 2 drawers for consoles with bowl | Vanity unit 980/550 with 2 drawers for consoles with bowl-54080000-Natural Oak-CHROME-400 | Natural Oak | 54080XXX | CHROME | 37.4 |
| Vanity unit 980_550 with 2 drawers for consoles with bowl-54080670-Natural Oak-MATT_BLACK-200 | 54080670 | Vanity unit 980/550 with 2 drawers for consoles with bowl | 4059625456750 | 980 | Vanity unit 980/550 with 2 drawers for consoles with bowl-54080670-Natural Oak-MATT_BLACK-200 | 200 | Vanity unit 980/550 with 2 drawers for consoles with bowl-54080670-Natural Oak-MATT_BLACK-200 | Xelu Q Vanity unit Natural Oak 980/550 with 2 drawers for consoles with bowl | Vanity unit 980/550 with 2 drawers for consoles with bowl-54080670-Natural Oak-MATT_BLACK-200 | Natural Oak | 54080XXX | MATT_BLACK | 37.4 |
| Vanity unit 980_550 with 2 drawers for consoles with bowl-54080670-Natural Oak-MATT_BLACK-400 | 54080670 | Vanity unit 980/550 with 2 drawers for consoles with bowl | 4059625456750 | 980 | Vanity unit 980/550 with 2 drawers for consoles with bowl-54080670-Natural Oak-MATT_BLACK-400 | 400 | Vanity unit 980/550 with 2 drawers for consoles with bowl-54080670-Natural Oak-MATT_BLACK-400 | Xelu Q Vanity unit Natural Oak 980/550 with 2 drawers for consoles with bowl | Vanity unit 980/550 with 2 drawers for consoles with bowl-54080670-Natural Oak-MATT_BLACK-400 | Natural Oak | 54080XXX | MATT_BLACK | 37.4 |
| Vanity unit 980_550 with 2 drawers for consoles with bowl-54080700-Natural Oak-MATT_WHITE-200 | 54080700 | Vanity unit 980/550 with 2 drawers for consoles with bowl | 4059625456750 | 980 | Vanity unit 980/550 with 2 drawers for consoles with bowl-54080700-Natural Oak-MATT_WHITE-200 | 200 | Vanity unit 980/550 with 2 drawers for consoles with bowl-54080700-Natural Oak-MATT_WHITE-200 | Xelu Q Vanity unit Natural Oak 980/550 with 2 drawers for consoles with bowl | Vanity unit 980/550 with 2 drawers for consoles with bowl-54080700-Natural Oak-MATT_WHITE-200 | Natural Oak | 54080XXX | MATT_WHITE | 37.4 |
| Vanity unit 980_550 with 2 drawers for consoles with bowl-54080700-Natural Oak-MATT_WHITE-400 | 54080700 | Vanity unit 980/550 with 2 drawers for consoles with bowl | 4059625456750 | 980 | Vanity unit 980/550 with 2 drawers for consoles with bowl-54080700-Natural Oak-MATT_WHITE-400 | 400 | Vanity unit 980/550 with 2 drawers for consoles with bowl-54080700-Natural Oak-MATT_WHITE-400 | Xelu Q Vanity unit Natural Oak 980/550 with 2 drawers for consoles with bowl | Vanity unit 980/550 with 2 drawers for consoles with bowl-54080700-Natural Oak-MATT_WHITE-400 | Natural Oak | 54080XXX | MATT_WHITE | 37.4 |
| Vanity unit 980_550 with 2 drawers for consoles with bowl-54081000-Dark Walnut-CHROME-200 | 54081000 | Vanity unit 980/550 with 2 drawers for consoles with bowl | 4059625456729 | 980 | Vanity unit 980/550 with 2 drawers for consoles with bowl-54081000-Dark Walnut-CHROME-200 | 200 | Vanity unit 980/550 with 2 drawers for consoles with bowl-54081000-Dark Walnut-CHROME-200 | Xelu Q Vanity unit Dark Walnut 980/550 with 2 drawers for consoles with bowl | Vanity unit 980/550 with 2 drawers for consoles with bowl-54081000-Dark Walnut-CHROME-200 | Dark Walnut | 54081XXX | CHROME | 37.4 |
| Vanity unit 980_550 with 2 drawers for consoles with bowl-54081000-Dark Walnut-CHROME-400 | 54081000 | Vanity unit 980/550 with 2 drawers for consoles with bowl | 4059625456729 | 980 | Vanity unit 980/550 with 2 drawers for consoles with bowl-54081000-Dark Walnut-CHROME-400 | 400 | Vanity unit 980/550 with 2 drawers for consoles with bowl-54081000-Dark Walnut-CHROME-400 | Xelu Q Vanity unit Dark Walnut 980/550 with 2 drawers for consoles with bowl | Vanity unit 980/550 with 2 drawers for consoles with bowl-54081000-Dark Walnut-CHROME-400 | Dark Walnut | 54081XXX | CHROME | 37.4 |
| Vanity unit 980_550 with 2 drawers for consoles with bowl-54081670-Dark Walnut-MATT_BLACK-200 | 54081670 | Vanity unit 980/550 with 2 drawers for consoles with bowl | 4059625456729 | 980 | Vanity unit 980/550 with 2 drawers for consoles with bowl-54081670-Dark Walnut-MATT_BLACK-200 | 200 | Vanity unit 980/550 with 2 drawers for consoles with bowl-54081670-Dark Walnut-MATT_BLACK-200 | Xelu Q Vanity unit Dark Walnut 980/550 with 2 drawers for consoles with bowl | Vanity unit 980/550 with 2 drawers for consoles with bowl-54081670-Dark Walnut-MATT_BLACK-200 | Dark Walnut | 54081XXX | MATT_BLACK | 37.4 |
| Vanity unit 980_550 with 2 drawers for consoles with bowl-54081670-Dark Walnut-MATT_BLACK-400 | 54081670 | Vanity unit 980/550 with 2 drawers for consoles with bowl | 4059625456729 | 980 | Vanity unit 980/550 with 2 drawers for consoles with bowl-54081670-Dark Walnut-MATT_BLACK-400 | 400 | Vanity unit 980/550 with 2 drawers for consoles with bowl-54081670-Dark Walnut-MATT_BLACK-400 | Xelu Q Vanity unit Dark Walnut 980/550 with 2 drawers for consoles with bowl | Vanity unit 980/550 with 2 drawers for consoles with bowl-54081670-Dark Walnut-MATT_BLACK-400 | Dark Walnut | 54081XXX | MATT_BLACK | 37.4 |
| Vanity unit 980_550 with 2 drawers for consoles with bowl-54081700-Dark Walnut-MATT_WHITE-200 | 54081700 | Vanity unit 980/550 with 2 drawers for consoles with bowl | 4059625456729 | 980 | Vanity unit 980/550 with 2 drawers for consoles with bowl-54081700-Dark Walnut-MATT_WHITE-200 | 200 | Vanity unit 980/550 with 2 drawers for consoles with bowl-54081700-Dark Walnut-MATT_WHITE-200 | Xelu Q Vanity unit Dark Walnut 980/550 with 2 drawers for consoles with bowl | Vanity unit 980/550 with 2 drawers for consoles with bowl-54081700-Dark Walnut-MATT_WHITE-200 | Dark Walnut | 54081XXX | MATT_WHITE | 37.4 |
| Vanity unit 980_550 with 2 drawers for consoles with bowl-54081700-Dark Walnut-MATT_WHITE-400 | 54081700 | Vanity unit 980/550 with 2 drawers for consoles with bowl | 4059625456729 | 980 | Vanity unit 980/550 with 2 drawers for consoles with bowl-54081700-Dark Walnut-MATT_WHITE-400 | 400 | Vanity unit 980/550 with 2 drawers for consoles with bowl-54081700-Dark Walnut-MATT_WHITE-400 | Xelu Q Vanity unit Dark Walnut 980/550 with 2 drawers for consoles with bowl | Vanity unit 980/550 with 2 drawers for consoles with bowl-54081700-Dark Walnut-MATT_WHITE-400 | Dark Walnut | 54081XXX | MATT_WHITE | 37.4 |

type visibility flags: 72 boolean params named "<type name>_RX0RY0RZ0TX0TY0TZ0_V" — each type sets only its own to Yes (folded from table)

## geometry (parser evidence)
native form markers: Sweep x105
no freeform markers — native parametric forms only
